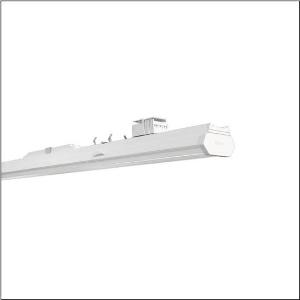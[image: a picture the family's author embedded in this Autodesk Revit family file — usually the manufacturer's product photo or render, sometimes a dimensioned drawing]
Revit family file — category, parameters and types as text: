
# Revit family: licross_11_protected_mo_51td1bdn49xg3s4
name_source: partatom
category: Lighting Fixtures
units: mm (PartAtom-declared; Revit-internal decimal feet)

## family parameters
Cut with Voids When Loaded = No
Host = Face
Light Source = No
Part Type = Normal
Room Calculation Point = No
Round Connector Dimension = Use Diameter
Shared = No

## types (1)
- --- (1 x LED, 920 lm, 6.8 W, 4000K)
    Apparent Load = 7 VA
    CIE Flux Codes = 54 82 95 97 100
    Color Rendering = 80
    Color Temperature = 4000K
    Default Elevation = 1800 mm
    Description = Licross 11 Protected MO, luminaire insert, of sheet steel, galvanised, coil coated, white, length: 1.500mm, width: 90mm, height: 101mm, LED rated luminous flux: 9.370lm, light colour: 840, SDCM (Standard Deviation of Colour Matching)MacAdam ≤ 2 SDCM (initial), control gear: DALI 2, with plug, 6-pole, with phase selection, for trunking rail, 9 or 11-core, mains connection: 220..240V, AC, 50/60Hz, rated input power: 61W, for trunking rail, 9-/11-core, internal wiring halogen-free, for emergency light function, converter,control gear: single battery element, battery: LiFePO4, 9Ah, primary optical cover: cover, of PMMA, light emission: direct distribution, primary light characteristic: symmetric, protection rating (complete): IP54, insulation class (complete): insulation class I (protective earthing), certification: CE, UKCA, protection symbol: D if used in an environment with non-conductive dust loads with corresponding accessories, impact resistance: IK06, permissible ambient temperature for indoor applications: +5..+35°C, standard: EN 60598-2-22, LABS conformity tested according to VDMA 24364:2018-05, reducing of maximum allowable ambient temperature of 5°C with ceiling mounting, corresponds to IFS (International Featured Standards) requirements for safety and quality in the food industry, The light source and the operating device comply with the requirements of the Ecodesign Regulation (EU) 2019/2020 and are replaceable in accordance with this regulation, packaging unit: 1 piece
    Height = 92 mm
    Lamp = 1 x LED
    Lamp Light Flux = 920 lm
    Lamp Power = 6.8 W
    Lamp count = 1
    Length = 1500 mm
    Luminous efficacy = 135 lm/W
    Manufacturer = Siteco
    ModVariant = No
    Model = 51TD1BDN49XG3S4
    Mounting Place = Ceiling
    Mounting Type = Pendant
    Number of Poles = 1
    OnlyDefault = Yes
    Power Factor = 1
    Product Name = Licross 11 Protected MO
    Product group = luminaire insert | ceiling pendant
    ProductGroupID = 901
    Protection Class = Protection class I
    Protection Degree = IP 54
    RLX_Detail_Level = 1
    RLX_Emergency_Light_Flux = 0 lm
    RLX_Emergency_Type = 0
    RLX_Emergency_Type_DB = No
    RlxData = <blob elided: 24965 chars, md5=a6946033>
    Socket = socket
    Standby Power = 0 W
    System Light Flux = 920 lm
    System Power = 7 W
    Type Comments = : emergency light operation: 3 h
    Type Image = l_1256145.jpg
    URL = http://relux.com
    VarID = @adj_096519
    Voltage = 0 V
    Weight = 0.00 kg
    Width = 88 mm

## geometry (parser evidence)
native form markers: Blend x4, Sweep x13
no freeform markers — native parametric forms only
